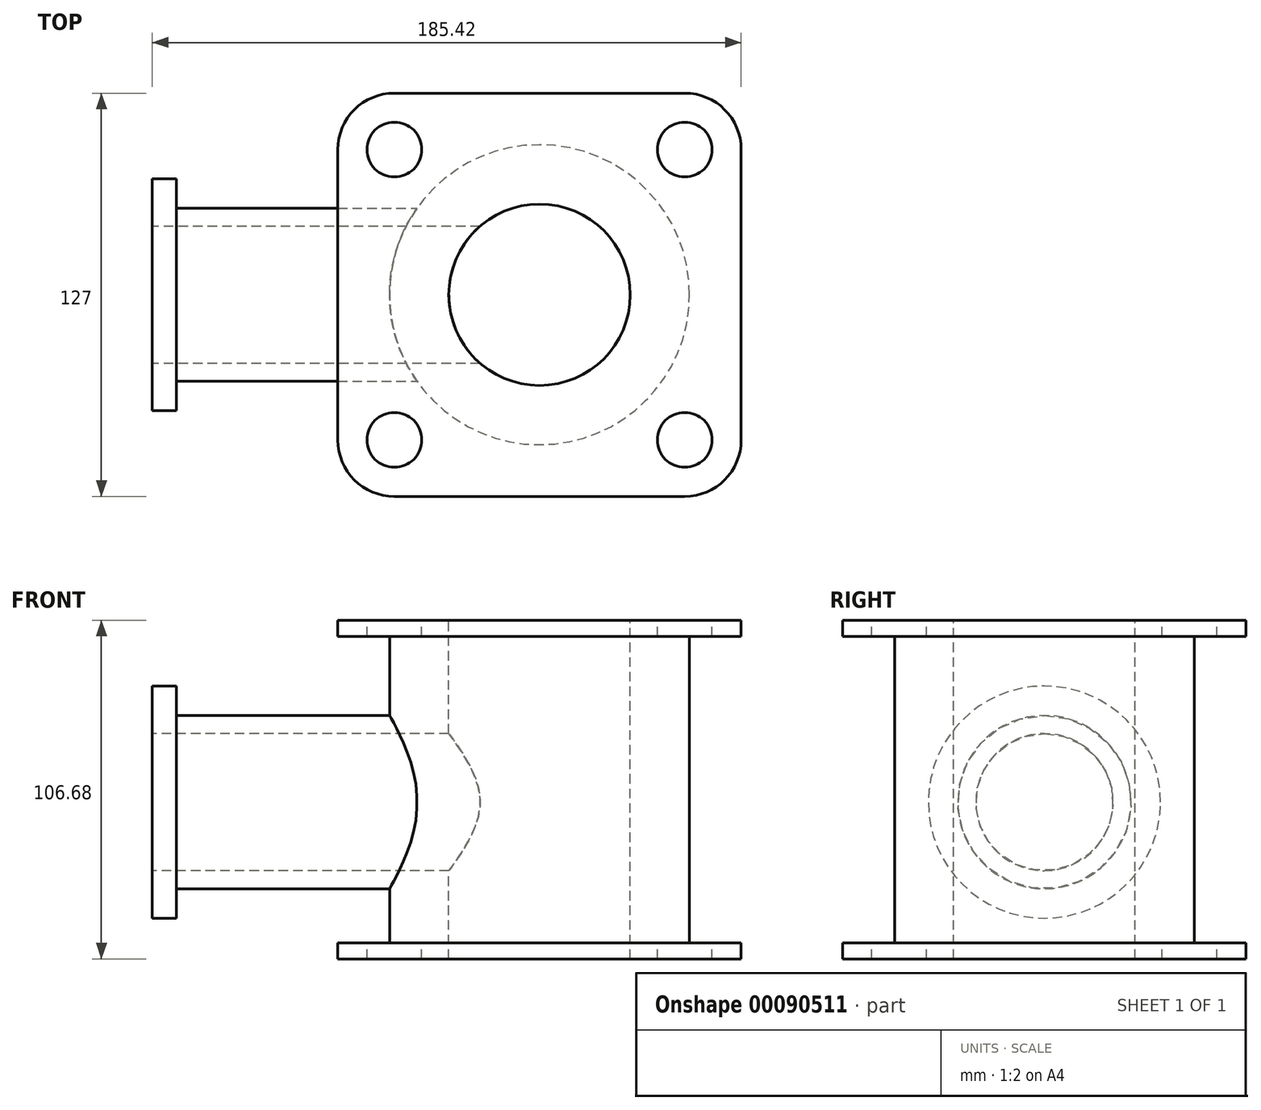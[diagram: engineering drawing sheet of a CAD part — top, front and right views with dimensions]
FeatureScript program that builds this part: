
annotation { "Feature Type Name" : "Feature", "Feature Type Description" : "" }
export const myFeature = defineFeature(function(context is Context, id is Id, definition is map)
    precondition{}
    {
        {
            var Q0;
            Q0=qCreatedBy(makeId("Top.planeOp"),FACE);
            var sketch = newSketch(context, id + "F0", { "sketchPlane" : qUnion([Q0])});
            skLineSegment(sketch, "E0.bottom", {"start": v(-63.5, 63.5) * mm, "end": v(63.5, 63.5) * mm});
            skLineSegment(sketch, "E0.top", {"start": v(-63.5, -63.5) * mm, "end": v(63.5, -63.5) * mm});
            skLineSegment(sketch, "E0.left", {"start": v(-63.5, 63.5) * mm, "end": v(-63.5, -63.5) * mm});
            skLineSegment(sketch, "E0.right", {"start": v(63.5, 63.5) * mm, "end": v(63.5, -63.5) * mm});
            skPoint(sketch, "E0.middle", {"position": v(0, 0) * mm});
            skSolve(sketch);
        }
        {
            var Q0;
            Q0 = qSketchRegion(id + "F0", true);
            extrude(context, id + "F1", {"entities" : qUnion([Q0]), "endBound" : BoundingType.SYMMETRIC, "depth" : 5.08 * mm});
        }
        {
            var Q0;
            Q0=makeQuery(id+"F1.opExtrude","CAP_FACE",FACE,{"disambiguationData":[OSD([sQuery(id+"F0.wireOp",EDGE,"E0.bottom"),sQuery(id+"F0.wireOp",EDGE,"E0.top"),sQuery(id+"F0.wireOp",EDGE,"E0.left"),sQuery(id+"F0.wireOp",EDGE,"E0.right")])],"isStart":false});
            var sketch = newSketch(context, id + "F2", { "sketchPlane" : qUnion([Q0])});
            skCircle(sketch, "E1", {"center": v(0, 0) * mm, "radius": 47.23 * mm});
            skSolve(sketch);
        }
        {
            var Q0;
            Q0 = qSketchRegion(id + "F2", true);
            extrude(context, id + "F3", {"entities" : qUnion([Q0]), "operationType" : NewBodyOperationType.ADD, "depth" : 101.6 * mm});
        }
        {
            var Q0;
            Q0=makeQuery(id+"F3.opExtrude","CAP_FACE",FACE,{"disambiguationData":[OSD([sQuery(id+"F2.wireOp",EDGE,"E1")])],"isStart":false});
            var sketch = newSketch(context, id + "F4", { "sketchPlane" : qUnion([Q0])});
            skLineSegment(sketch, "E2.bottom", {"start": v(63.5, 63.5) * mm, "end": v(-63.5, 63.5) * mm});
            skLineSegment(sketch, "E2.top", {"start": v(63.5, -63.5) * mm, "end": v(-63.5, -63.5) * mm});
            skLineSegment(sketch, "E2.left", {"start": v(63.5, 63.5) * mm, "end": v(63.5, -63.5) * mm});
            skLineSegment(sketch, "E2.right", {"start": v(-63.5, 63.5) * mm, "end": v(-63.5, -63.5) * mm});
            skPoint(sketch, "E2.middle", {"position": v(0, 0) * mm});
            skSolve(sketch);
        }
        {
            var Q0;
            Q0=makeQuery(id+"F4.imprint","IMPRINT",FACE,{"disambiguationData":[TD([[makeQuery(id+"F4.imprint","IMPRINT",EDGE,{"derivedFrom":sQuery(id+"F4.wireOp",EDGE,"E2.bottom")}),1.0]])]});
            extrude(context, id + "F5", {"entities" : qUnion([Q0]), "operationType" : NewBodyOperationType.ADD, "oppositeDirection" : true, "depth" : 5.08 * mm});
        }
        {
            var Q0;
            Q0=makeQuery(id+"F1.opExtrude","SWEPT_FACE",FACE,{"disambiguationData":[OSD([sQuery(id+"F0.wireOp",EDGE,"E0.left")])]});
            var sketch = newSketch(context, id + "F6", { "sketchPlane" : qUnion([Q0])});
            skCircle(sketch, "E3", {"center": v(0, 46.83) * mm, "radius": 27.29 * mm});
            skSolve(sketch);
        }
        {
            var Q0;
            Q0 = qSketchRegion(id + "F6", true);
            extrude(context, id + "F7", {"entities" : qUnion([Q0]), "operationType" : NewBodyOperationType.ADD, "endBound" : BoundingType.SYMMETRIC, "depth" : 101.6 * mm});
        }
        {
            var Q0;
            {var subQ0=sQuery(id+"F2.wireOp",EDGE,"E1");Q0=makeQuery(id+"F5.boolean.opBoolean","MERGE",FACE,{"derivedFrom":[makeQuery(id+"F3.opExtrude","CAP_FACE",FACE,{"disambiguationData":[OSD([subQ0])],"isStart":false}),makeQuery(id+"F5.opExtrude","CAP_FACE",FACE,{"disambiguationData":[OSD([subQ0,sQuery(id+"F4.wireOp",EDGE,"E2.bottom"),sQuery(id+"F4.wireOp",EDGE,"E2.top"),sQuery(id+"F4.wireOp",EDGE,"E2.left"),sQuery(id+"F4.wireOp",EDGE,"E2.right")])],"isStart":true})]});}
            var sketch = newSketch(context, id + "F8", { "sketchPlane" : qUnion([Q0])});
            skPoint(sketch, "E4", {"position": v(0, 0) * mm});
            skSolve(sketch);
        }
        {
            var Q0;
            Q0=sQuery(id+"F8.wireOp",VERTEX,"E4");
            var Q1;
            Q1=makeQuery(id+"F1.opExtrude","SWEPT_BODY",BODY,{"disambiguationData":[OSD([sQuery(id+"F0.wireOp",EDGE,"E0.bottom"),sQuery(id+"F0.wireOp",EDGE,"E0.top"),sQuery(id+"F0.wireOp",EDGE,"E0.left"),sQuery(id+"F0.wireOp",EDGE,"E0.right")])]});
            hole(context, id + "F9", {"style" : HoleStyle.SIMPLE, "endStyle" : HoleEndStyle.THROUGH, "holeDiameter" : 57.15 * mm, "locations" : qUnion([Q0]), "scope" : qUnion([Q1]), "isTappedThrough" : true});
        }
        {
            var Q0;
            Q0=makeQuery(id+"F5.opExtrude","SWEPT_EDGE",EDGE,{"disambiguationData":[OSD([sQuery(id+"F4.wireOp",EDGE,"E2.top"),sQuery(id+"F4.wireOp",EDGE,"E2.right")])]});
            var Q1;
            Q1=makeQuery(id+"F5.opExtrude","SWEPT_EDGE",EDGE,{"disambiguationData":[OSD([sQuery(id+"F4.wireOp",EDGE,"E2.top"),sQuery(id+"F4.wireOp",EDGE,"E2.left")])]});
            var Q2;
            Q2=makeQuery(id+"F1.opExtrude","SWEPT_EDGE",EDGE,{"disambiguationData":[OSD([sQuery(id+"F0.wireOp",EDGE,"E0.top"),sQuery(id+"F0.wireOp",EDGE,"E0.right")])]});
            var Q3;
            Q3=makeQuery(id+"F1.opExtrude","SWEPT_EDGE",EDGE,{"disambiguationData":[OSD([sQuery(id+"F0.wireOp",EDGE,"E0.top"),sQuery(id+"F0.wireOp",EDGE,"E0.left")])]});
            var Q4;
            Q4=makeQuery(id+"F5.opExtrude","SWEPT_EDGE",EDGE,{"disambiguationData":[OSD([sQuery(id+"F4.wireOp",EDGE,"E2.bottom"),sQuery(id+"F4.wireOp",EDGE,"E2.right")])]});
            var Q5;
            Q5=makeQuery(id+"F1.opExtrude","SWEPT_EDGE",EDGE,{"disambiguationData":[OSD([sQuery(id+"F0.wireOp",EDGE,"E0.bottom"),sQuery(id+"F0.wireOp",EDGE,"E0.left")])]});
            var Q6;
            Q6=makeQuery(id+"F5.opExtrude","SWEPT_EDGE",EDGE,{"disambiguationData":[OSD([sQuery(id+"F4.wireOp",EDGE,"E2.bottom"),sQuery(id+"F4.wireOp",EDGE,"E2.left")])]});
            var Q7;
            Q7=makeQuery(id+"F1.opExtrude","SWEPT_EDGE",EDGE,{"disambiguationData":[OSD([sQuery(id+"F0.wireOp",EDGE,"E0.bottom"),sQuery(id+"F0.wireOp",EDGE,"E0.right")])]});
            fillet(context, id + "F10", {"entities" : qUnion([Q0, Q1, Q2, Q3, Q4, Q5, Q6, Q7]), "radius" : 17.78 * mm, "tangentPropagation" : true, "allowEdgeOverflow" : false});
        }
        {
            var Q0;
            {var subQ0=sQuery(id+"F2.wireOp",EDGE,"E1");Q0=makeQuery(id+"F5.boolean.opBoolean","MERGE",FACE,{"derivedFrom":[makeQuery(id+"F3.opExtrude","CAP_FACE",FACE,{"disambiguationData":[OSD([subQ0])],"isStart":false}),makeQuery(id+"F5.opExtrude","CAP_FACE",FACE,{"disambiguationData":[OSD([subQ0,sQuery(id+"F4.wireOp",EDGE,"E2.bottom"),sQuery(id+"F4.wireOp",EDGE,"E2.top"),sQuery(id+"F4.wireOp",EDGE,"E2.left"),sQuery(id+"F4.wireOp",EDGE,"E2.right")])],"isStart":true})]});}
            var sketch = newSketch(context, id + "F11", { "sketchPlane" : qUnion([Q0])});
            skCircle(sketch, "E5", {"center": v(-45.72, 45.72) * mm, "radius": 8.63 * mm});
            skCircle(sketch, "E6", {"center": v(45.72, 45.72) * mm, "radius": 8.63 * mm});
            skCircle(sketch, "E7", {"center": v(45.72, -45.72) * mm, "radius": 8.63 * mm});
            skCircle(sketch, "E8", {"center": v(-45.72, -45.72) * mm, "radius": 8.63 * mm});
            skSolve(sketch);
        }
        {
            var Q0;
            Q0 = qSketchRegion(id + "F11", true);
            extrude(context, id + "F12", {"entities" : qUnion([Q0]), "operationType" : NewBodyOperationType.REMOVE, "endBound" : BoundingType.THROUGH_ALL, "oppositeDirection" : true, "depth" : 25.4 * mm});
        }
        {
            var Q0;
            Q0=makeQuery(id+"F7.opExtrude","CAP_FACE",FACE,{"disambiguationData":[OSD([sQuery(id+"F6.wireOp",EDGE,"E3")])],"isStart":false});
            var sketch = newSketch(context, id + "F13", { "sketchPlane" : qUnion([Q0])});
            skCircle(sketch, "E9", {"center": v(0, 46.83) * mm, "radius": 36.56 * mm});
            skSolve(sketch);
        }
        {
            var Q0;
            Q0 = qSketchRegion(id + "F13", true);
            extrude(context, id + "F14", {"entities" : qUnion([Q0]), "operationType" : NewBodyOperationType.ADD, "depth" : 7.62 * mm});
        }
        {
            var Q0;
            Q0=makeQuery(id+"F14.opExtrude","CAP_FACE",FACE,{"disambiguationData":[OSD([sQuery(id+"F13.wireOp",EDGE,"E9")])],"isStart":false});
            var sketch = newSketch(context, id + "F15", { "sketchPlane" : qUnion([Q0])});
            skPoint(sketch, "E10", {"position": v(0, 46.83) * mm});
            skSolve(sketch);
        }
        {
            var Q0;
            Q0=sQuery(id+"F15.wireOp",VERTEX,"E10");
            var Q1;
            Q1=makeQuery(id+"F1.opExtrude","SWEPT_BODY",BODY,{"disambiguationData":[OSD([sQuery(id+"F0.wireOp",EDGE,"E0.bottom"),sQuery(id+"F0.wireOp",EDGE,"E0.top"),sQuery(id+"F0.wireOp",EDGE,"E0.left"),sQuery(id+"F0.wireOp",EDGE,"E0.right")])]});
            hole(context, id + "F16", {"style" : HoleStyle.SIMPLE, "endStyle" : HoleEndStyle.BLIND, "holeDiameter" : 43.18 * mm, "holeDepth" : 127 * mm, "locations" : qUnion([Q0]), "scope" : qUnion([Q1])});
        }
    });
